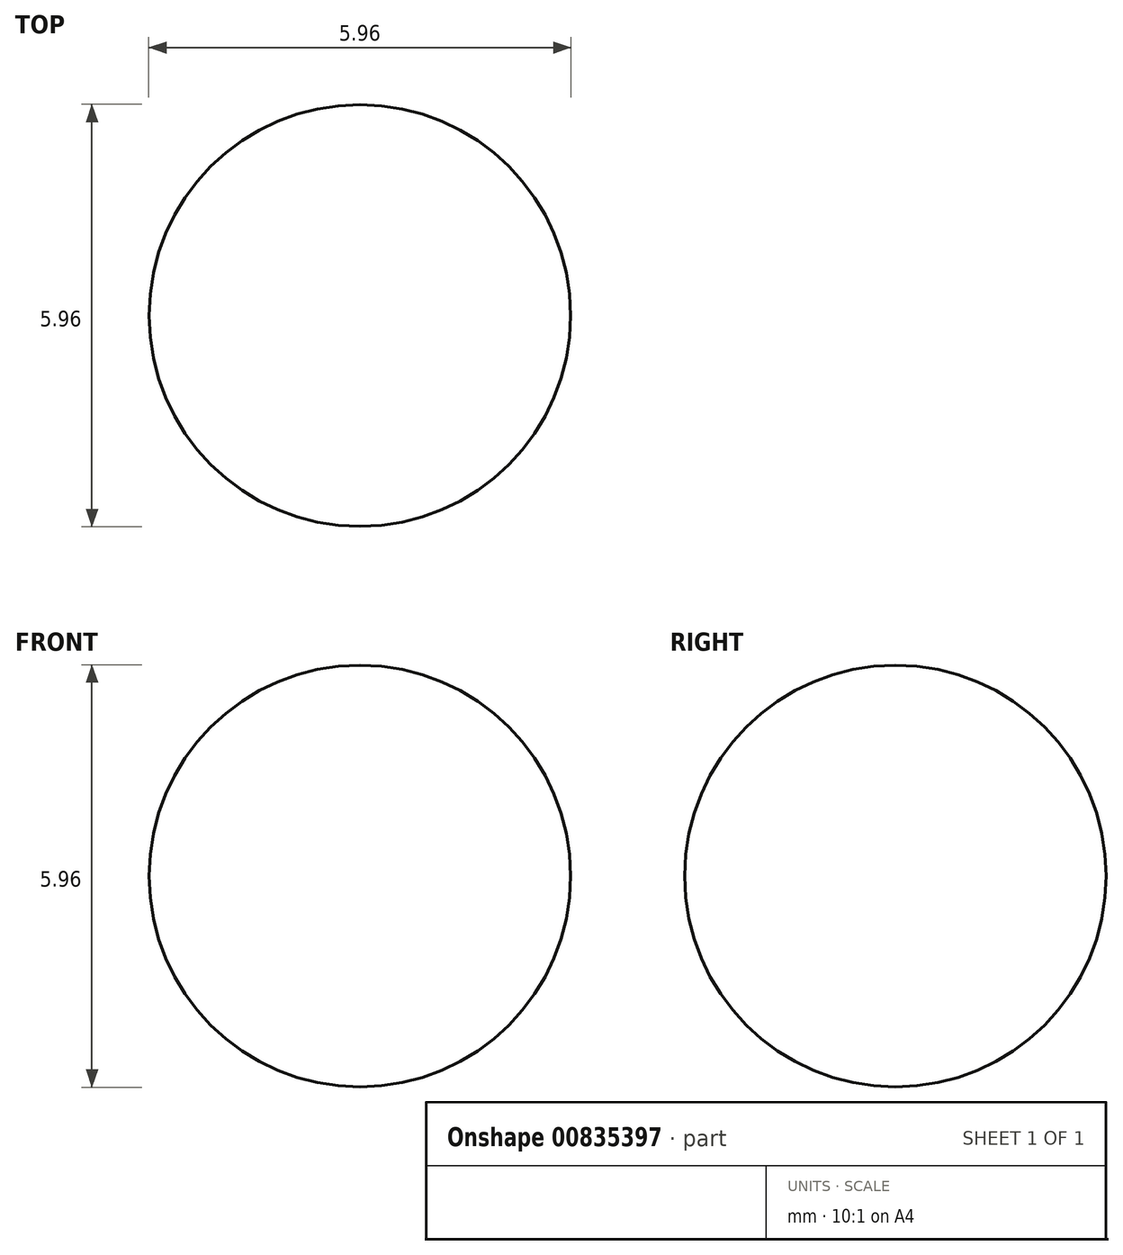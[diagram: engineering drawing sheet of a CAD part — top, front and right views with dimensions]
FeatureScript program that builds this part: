
annotation { "Feature Type Name" : "Feature", "Feature Type Description" : "" }
export const myFeature = defineFeature(function(context is Context, id is Id, definition is map)
    precondition{}
    {
        {
            var Q0;
            Q0=qCreatedBy(makeId("Front.planeOp"),FACE);
            var sketch = newSketch(context, id + "F0", { "sketchPlane" : qUnion([Q0])});
            skArc(sketch, "E0", {"start": v(0, -2.98) * mm, "mid": v(2.98, 0) * mm, "end": v(0, 2.98) * mm});
            skLineSegment(sketch, "E1", {"start": v(0, 2.98) * mm, "end": v(0, -2.98) * mm});
            skSolve(sketch);
        }
        {
            var Q0;
            Q0 = qSketchRegion(id + "F0", true);
            var Q1;
            Q1=sQuery(id+"F0.wireOp",EDGE,"E1");
            revolve(context, id + "F1", {"surfaceOperationType" : NewSurfaceOperationType.NEW, "entities" : qUnion([Q0]), "axis" : qUnion([Q1]), "revolveType" : RevolveType.FULL});
        }
    });
